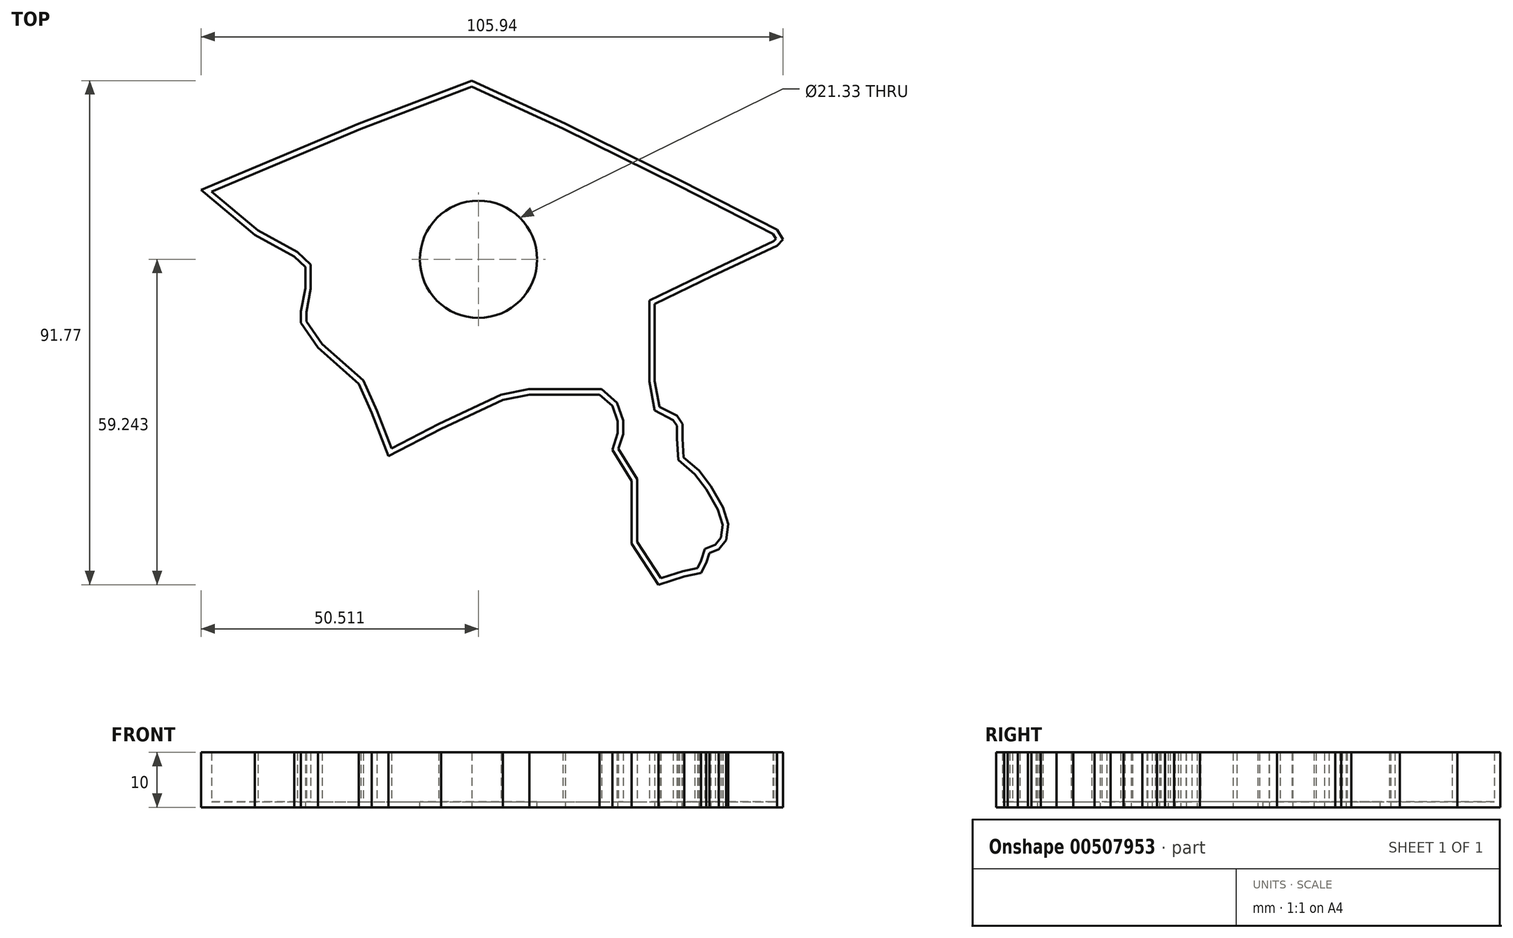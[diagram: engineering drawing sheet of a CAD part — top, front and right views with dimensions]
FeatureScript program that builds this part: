
annotation { "Feature Type Name" : "Feature", "Feature Type Description" : "" }
export const myFeature = defineFeature(function(context is Context, id is Id, definition is map)
    precondition{}
    {
        {
            var Q0;
            Q0=qCreatedBy(makeId("Top.planeOp"),FACE);
            var sketch = newSketch(context, id + "F0", { "sketchPlane" : qUnion([Q0])});
            skLineSegment(sketch, "E0", {"start": v(-59.76, 20.74) * mm, "end": v(-31.03, 32.82) * mm});
            skLineSegment(sketch, "E1", {"start": v(-31.03, 32.82) * mm, "end": v(-10.45, 40.66) * mm});
            skLineSegment(sketch, "E2", {"start": v(-10.45, 40.66) * mm, "end": v(6.53, 32.82) * mm});
            skLineSegment(sketch, "E3", {"start": v(6.53, 32.82) * mm, "end": v(27.76, 22.37) * mm});
            skLineSegment(sketch, "E4", {"start": v(27.76, 22.37) * mm, "end": v(45.07, 13.55) * mm});
            skLineSegment(sketch, "E5", {"start": v(45.07, 10.61) * mm, "end": v(33.31, 5.06) * mm});
            skLineSegment(sketch, "E6", {"start": v(33.31, 5.06) * mm, "end": v(22.83, 0) * mm});
            skLineSegment(sketch, "E7", {"start": v(22.83, 0) * mm, "end": v(22.83, -14) * mm});
            skLineSegment(sketch, "E8", {"start": v(-49.97, 12.57) * mm, "end": v(-59.76, 20.74) * mm});
            skLineSegment(sketch, "E9", {"start": v(-42.78, 8.65) * mm, "end": v(-49.97, 12.57) * mm});
            skLineSegment(sketch, "E10", {"start": v(-38.49, -7.97) * mm, "end": v(-31.01, -14.51) * mm});
            skLineSegment(sketch, "E11", {"start": v(0, -16.5) * mm, "end": v(12.77, -16.5) * mm});
            skLineSegment(sketch, "E12", {"start": v(18.62, -43.6) * mm, "end": v(18.62, -32.17) * mm});
            skLineSegment(sketch, "E13", {"start": v(18.62, -43.6) * mm, "end": v(23.51, -51.11) * mm});
            skLineSegment(sketch, "E14", {"start": v(-42.78, 8.65) * mm, "end": v(-40.78, 6.73) * mm});
            skLineSegment(sketch, "E15", {"start": v(12.77, -16.5) * mm, "end": v(15.1, -18.53) * mm});
            skLineSegment(sketch, "E16", {"start": v(15.1, -26.52) * mm, "end": v(18.62, -32.17) * mm});
            skLineSegment(sketch, "E17", {"start": v(-40.78, 6.73) * mm, "end": v(-40.78, 2.86) * mm});
            skLineSegment(sketch, "E18", {"start": v(-40.78, 2.86) * mm, "end": v(-41.56, -1.37) * mm});
            skLineSegment(sketch, "E19", {"start": v(-41.56, -1.37) * mm, "end": v(-41.56, -3.46) * mm});
            skLineSegment(sketch, "E20", {"start": v(-41.56, -3.46) * mm, "end": v(-38.49, -7.97) * mm});
            skLineSegment(sketch, "E21", {"start": v(45.07, 13.55) * mm, "end": v(46.18, 11.74) * mm});
            skLineSegment(sketch, "E22", {"start": v(46.18, 11.74) * mm, "end": v(45.07, 10.61) * mm});
            skLineSegment(sketch, "E23", {"start": v(15.1, -18.53) * mm, "end": v(16.08, -21.37) * mm});
            skLineSegment(sketch, "E24", {"start": v(16.08, -21.37) * mm, "end": v(16.08, -23.5) * mm});
            skLineSegment(sketch, "E25", {"start": v(16.08, -23.5) * mm, "end": v(15.1, -26.52) * mm});
            skLineSegment(sketch, "E26", {"start": v(-31.01, -14.51) * mm, "end": v(-28.68, -19.82) * mm});
            skLineSegment(sketch, "E27", {"start": v(-28.68, -19.82) * mm, "end": v(-26.08, -26.52) * mm});
            skLineSegment(sketch, "E28", {"start": v(-26.08, -26.52) * mm, "end": v(-25.63, -27.68) * mm});
            skLineSegment(sketch, "E29", {"start": v(-25.63, -27.68) * mm, "end": v(-16.06, -22.73) * mm});
            skLineSegment(sketch, "E30", {"start": v(-16.06, -22.73) * mm, "end": v(-4.8, -17.49) * mm});
            skLineSegment(sketch, "E31", {"start": v(-4.8, -17.49) * mm, "end": v(0, -16.5) * mm});
            skLineSegment(sketch, "E32", {"start": v(22.83, -14) * mm, "end": v(23.72, -18.73) * mm});
            skLineSegment(sketch, "E33", {"start": v(23.72, -18.73) * mm, "end": v(26.84, -20.35) * mm});
            skLineSegment(sketch, "E34", {"start": v(26.84, -20.35) * mm, "end": v(27.88, -21.85) * mm});
            skLineSegment(sketch, "E35", {"start": v(27.88, -21.85) * mm, "end": v(27.88, -24.5) * mm});
            skLineSegment(sketch, "E36", {"start": v(27.88, -24.5) * mm, "end": v(28.09, -27.92) * mm});
            skLineSegment(sketch, "E37", {"start": v(23.51, -51.11) * mm, "end": v(25.84, -50.37) * mm});
            skLineSegment(sketch, "E38", {"start": v(25.84, -50.37) * mm, "end": v(28.2, -49.62) * mm});
            skLineSegment(sketch, "E39", {"start": v(28.2, -49.62) * mm, "end": v(31.27, -48.98) * mm});
            skLineSegment(sketch, "E40", {"start": v(31.27, -48.98) * mm, "end": v(32.2, -47.14) * mm});
            skLineSegment(sketch, "E41", {"start": v(32.2, -47.14) * mm, "end": v(32.77, -45.35) * mm});
            skLineSegment(sketch, "E42", {"start": v(32.77, -45.35) * mm, "end": v(34.5, -44.65) * mm});
            skLineSegment(sketch, "E43", {"start": v(34.5, -44.65) * mm, "end": v(35.83, -42.98) * mm});
            skLineSegment(sketch, "E44", {"start": v(35.83, -42.98) * mm, "end": v(36.23, -40.1) * mm});
            skLineSegment(sketch, "E45", {"start": v(36.23, -40.1) * mm, "end": v(35.25, -37.03) * mm});
            skLineSegment(sketch, "E46", {"start": v(35.25, -37.03) * mm, "end": v(33.06, -33.17) * mm});
            skLineSegment(sketch, "E47", {"start": v(33.06, -33.17) * mm, "end": v(30.86, -30.28) * mm});
            skLineSegment(sketch, "E48", {"start": v(30.86, -30.28) * mm, "end": v(28.09, -27.92) * mm});
            skSolve(sketch);
        }
        {
            var Q0;
            Q0=makeQuery(id+"F0.imprint","IMPRINT",FACE,{"disambiguationData":[TD([[makeQuery(id+"F0.imprint","IMPRINT",EDGE,{"derivedFrom":sQuery(id+"F0.wireOp",EDGE,"E0")}),-1.0]])]});
            extrude(context, id + "F1", {"entities" : qUnion([Q0]), "depth" : 10 * mm});
        }
        {
            var Q0;
            Q0=makeQuery(id+"F1.opExtrude","CAP_FACE",FACE,{"disambiguationData":[OSD([sQuery(id+"F0.wireOp",EDGE,"E0"),sQuery(id+"F0.wireOp",EDGE,"E1"),sQuery(id+"F0.wireOp",EDGE,"E2"),sQuery(id+"F0.wireOp",EDGE,"E3"),sQuery(id+"F0.wireOp",EDGE,"E4"),sQuery(id+"F0.wireOp",EDGE,"E5"),sQuery(id+"F0.wireOp",EDGE,"E6"),sQuery(id+"F0.wireOp",EDGE,"E7"),sQuery(id+"F0.wireOp",EDGE,"E8"),sQuery(id+"F0.wireOp",EDGE,"E9"),sQuery(id+"F0.wireOp",EDGE,"E10"),sQuery(id+"F0.wireOp",EDGE,"E11"),sQuery(id+"F0.wireOp",EDGE,"E12"),sQuery(id+"F0.wireOp",EDGE,"E13"),sQuery(id+"F0.wireOp",EDGE,"E14"),sQuery(id+"F0.wireOp",EDGE,"E15"),sQuery(id+"F0.wireOp",EDGE,"E16"),sQuery(id+"F0.wireOp",EDGE,"E17"),sQuery(id+"F0.wireOp",EDGE,"E18"),sQuery(id+"F0.wireOp",EDGE,"E19"),sQuery(id+"F0.wireOp",EDGE,"E20"),sQuery(id+"F0.wireOp",EDGE,"E21"),sQuery(id+"F0.wireOp",EDGE,"E22"),sQuery(id+"F0.wireOp",EDGE,"E23"),sQuery(id+"F0.wireOp",EDGE,"E24"),sQuery(id+"F0.wireOp",EDGE,"E25"),sQuery(id+"F0.wireOp",EDGE,"E26"),sQuery(id+"F0.wireOp",EDGE,"E27"),sQuery(id+"F0.wireOp",EDGE,"E28"),sQuery(id+"F0.wireOp",EDGE,"E29"),sQuery(id+"F0.wireOp",EDGE,"E30"),sQuery(id+"F0.wireOp",EDGE,"E31"),sQuery(id+"F0.wireOp",EDGE,"E32"),sQuery(id+"F0.wireOp",EDGE,"E33"),sQuery(id+"F0.wireOp",EDGE,"E34"),sQuery(id+"F0.wireOp",EDGE,"E35"),sQuery(id+"F0.wireOp",EDGE,"E36"),sQuery(id+"F0.wireOp",EDGE,"E37"),sQuery(id+"F0.wireOp",EDGE,"E38"),sQuery(id+"F0.wireOp",EDGE,"E39"),sQuery(id+"F0.wireOp",EDGE,"E40"),sQuery(id+"F0.wireOp",EDGE,"E41"),sQuery(id+"F0.wireOp",EDGE,"E42"),sQuery(id+"F0.wireOp",EDGE,"E43"),sQuery(id+"F0.wireOp",EDGE,"E44"),sQuery(id+"F0.wireOp",EDGE,"E45"),sQuery(id+"F0.wireOp",EDGE,"E46"),sQuery(id+"F0.wireOp",EDGE,"E47"),sQuery(id+"F0.wireOp",EDGE,"E48")])],"isStart":false});
            shell(context, id + "F2", {"entities" : qUnion([Q0]), "thickness" : 1 * mm});
        }
        {
            var Q0;
            Q0=makeQuery(id+"F2.opShell","OFFSET_FACE",FACE,{"disambiguationData":[OSD([sQuery(id+"F0.wireOp",EDGE,"E0"),sQuery(id+"F0.wireOp",EDGE,"E1"),sQuery(id+"F0.wireOp",EDGE,"E2"),sQuery(id+"F0.wireOp",EDGE,"E3"),sQuery(id+"F0.wireOp",EDGE,"E4"),sQuery(id+"F0.wireOp",EDGE,"E5"),sQuery(id+"F0.wireOp",EDGE,"E6"),sQuery(id+"F0.wireOp",EDGE,"E7"),sQuery(id+"F0.wireOp",EDGE,"E8"),sQuery(id+"F0.wireOp",EDGE,"E9"),sQuery(id+"F0.wireOp",EDGE,"E10"),sQuery(id+"F0.wireOp",EDGE,"E11"),sQuery(id+"F0.wireOp",EDGE,"E12"),sQuery(id+"F0.wireOp",EDGE,"E13"),sQuery(id+"F0.wireOp",EDGE,"E14"),sQuery(id+"F0.wireOp",EDGE,"E15"),sQuery(id+"F0.wireOp",EDGE,"E16"),sQuery(id+"F0.wireOp",EDGE,"E17"),sQuery(id+"F0.wireOp",EDGE,"E18"),sQuery(id+"F0.wireOp",EDGE,"E19"),sQuery(id+"F0.wireOp",EDGE,"E20"),sQuery(id+"F0.wireOp",EDGE,"E21"),sQuery(id+"F0.wireOp",EDGE,"E22"),sQuery(id+"F0.wireOp",EDGE,"E23"),sQuery(id+"F0.wireOp",EDGE,"E24"),sQuery(id+"F0.wireOp",EDGE,"E25"),sQuery(id+"F0.wireOp",EDGE,"E26"),sQuery(id+"F0.wireOp",EDGE,"E27"),sQuery(id+"F0.wireOp",EDGE,"E28"),sQuery(id+"F0.wireOp",EDGE,"E29"),sQuery(id+"F0.wireOp",EDGE,"E30"),sQuery(id+"F0.wireOp",EDGE,"E31"),sQuery(id+"F0.wireOp",EDGE,"E32"),sQuery(id+"F0.wireOp",EDGE,"E33"),sQuery(id+"F0.wireOp",EDGE,"E34"),sQuery(id+"F0.wireOp",EDGE,"E35"),sQuery(id+"F0.wireOp",EDGE,"E36"),sQuery(id+"F0.wireOp",EDGE,"E37"),sQuery(id+"F0.wireOp",EDGE,"E38"),sQuery(id+"F0.wireOp",EDGE,"E39"),sQuery(id+"F0.wireOp",EDGE,"E40"),sQuery(id+"F0.wireOp",EDGE,"E41"),sQuery(id+"F0.wireOp",EDGE,"E42"),sQuery(id+"F0.wireOp",EDGE,"E43"),sQuery(id+"F0.wireOp",EDGE,"E44"),sQuery(id+"F0.wireOp",EDGE,"E45"),sQuery(id+"F0.wireOp",EDGE,"E46"),sQuery(id+"F0.wireOp",EDGE,"E47"),sQuery(id+"F0.wireOp",EDGE,"E48")])]});
            var sketch = newSketch(context, id + "F3", { "sketchPlane" : qUnion([Q0])});
            skCircle(sketch, "E49", {"center": v(-9.25, 8.13) * mm, "radius": 10.66 * mm});
            skSolve(sketch);
        }
        {
            var Q0;
            Q0 = qSketchRegion(id + "F3", true);
            extrude(context, id + "F4", {"entities" : qUnion([Q0]), "operationType" : NewBodyOperationType.REMOVE, "oppositeDirection" : true, "depth" : 25 * mm});
        }
    });
